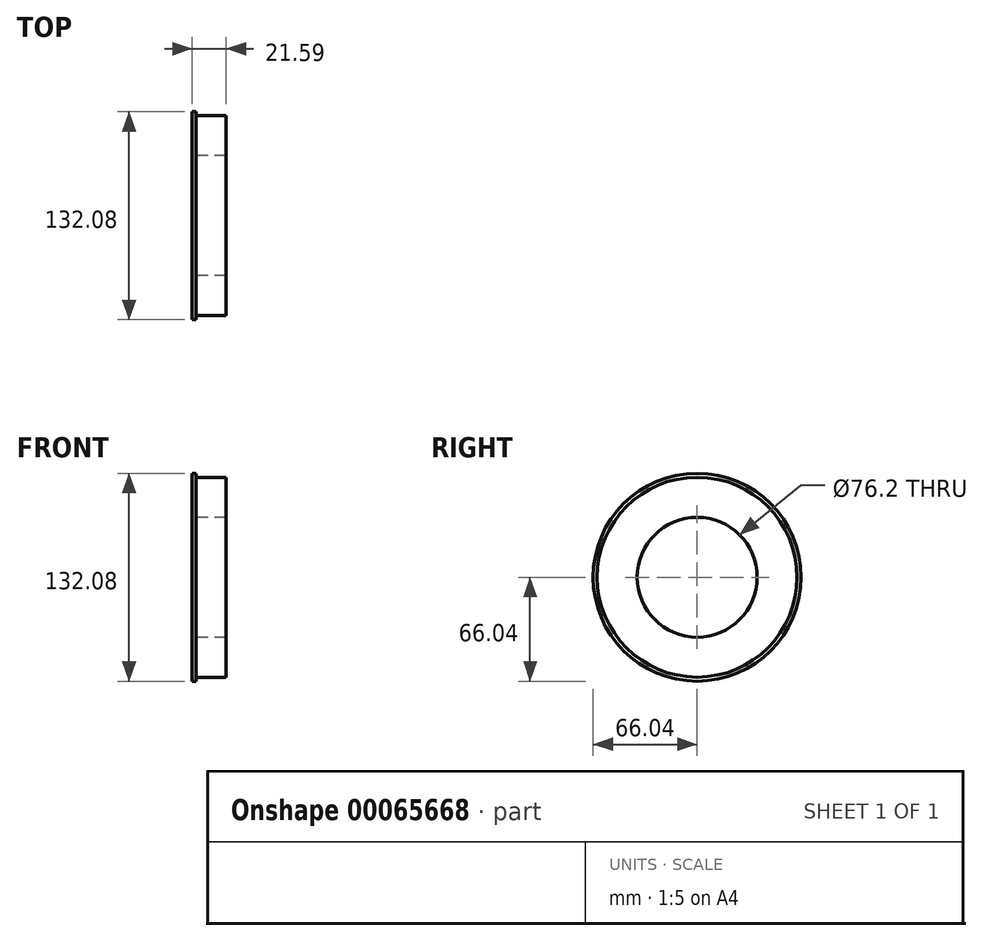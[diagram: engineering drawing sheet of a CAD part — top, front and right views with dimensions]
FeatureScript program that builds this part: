
annotation { "Feature Type Name" : "Feature", "Feature Type Description" : "" }
export const myFeature = defineFeature(function(context is Context, id is Id, definition is map)
    precondition{}
    {
        {
            var Q0;
            Q0=qCreatedBy(makeId("Right.planeOp"),FACE);
            var sketch = newSketch(context, id + "F0", { "sketchPlane" : qUnion([Q0])});
            skCircle(sketch, "E0", {"center": v(0, 0) * mm, "radius": 63.5 * mm});
            skCircle(sketch, "E1", {"center": v(0, 0) * mm, "radius": 38.1 * mm});
            skSolve(sketch);
        }
        {
            var Q0;
            Q0 = qSketchRegion(id + "F0", true);
            extrude(context, id + "F1", {"entities" : qUnion([Q0]), "depth" : 19.05 * mm});
        }
        {
            var Q0;
            Q0=makeQuery(id+"F1.opExtrude","CAP_FACE",FACE,{"disambiguationData":[OSD([sQuery(id+"F0.wireOp",EDGE,"E0"),sQuery(id+"F0.wireOp",EDGE,"E1")])],"isStart":true});
            var sketch = newSketch(context, id + "F2", { "sketchPlane" : qUnion([Q0])});
            skCircle(sketch, "E2", {"center": v(0, 0) * mm, "radius": 38.1 * mm});
            skCircle(sketch, "E3", {"center": v(0, 0) * mm, "radius": 66.04 * mm});
            skPoint(sketch, "E4", {"position": v(0, 63.5) * mm});
            skSolve(sketch);
        }
        {
            var Q0;
            Q0 = qSketchRegion(id + "F2", true);
            extrude(context, id + "F3", {"entities" : qUnion([Q0]), "operationType" : NewBodyOperationType.ADD, "depth" : 2.54 * mm});
        }
    });
